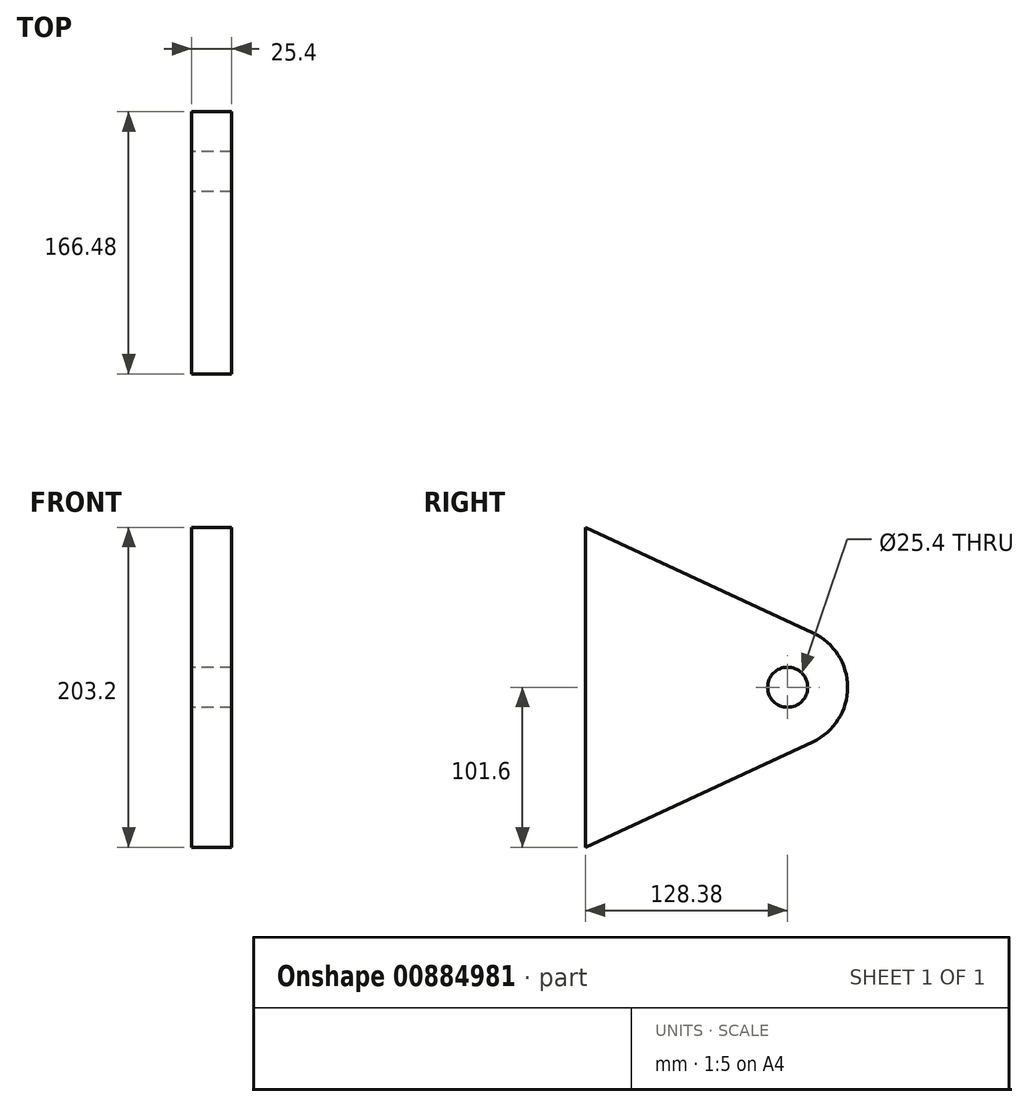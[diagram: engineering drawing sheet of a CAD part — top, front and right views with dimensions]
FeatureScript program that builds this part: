
annotation { "Feature Type Name" : "Feature", "Feature Type Description" : "" }
export const myFeature = defineFeature(function(context is Context, id is Id, definition is map)
    precondition{}
    {
        {
            var Q0;
            Q0=qCreatedBy(makeId("Right.planeOp"),FACE);
            var sketch = newSketch(context, id + "F0", { "sketchPlane" : qUnion([Q0])});
            skLineSegment(sketch, "E0", {"start": v(0, 101.6) * mm, "end": v(0, -101.6) * mm});
            skLineSegment(sketch, "E1", {"start": v(0, -101.6) * mm, "end": v(144.42, -34.56) * mm});
            skLineSegment(sketch, "E2", {"start": v(144.42, 34.56) * mm, "end": v(0, 101.6) * mm});
            skPoint(sketch, "E3.visualSharp", {"position": v(218.87, 0) * mm});
            skArc(sketch, "E3.filletArc", {"start": v(144.42, -34.56) * mm, "mid": v(166.48, 0) * mm, "end": v(144.42, 34.56) * mm});
            skCircle(sketch, "E4", {"center": v(128.38, 0) * mm, "radius": 12.7 * mm});
            skSolve(sketch);
        }
        {
            var Q0;
            Q0 = qSketchRegion(id + "F0", true);
            extrude(context, id + "F1", {"entities" : qUnion([Q0]), "depth" : 25.4 * mm, "offsetDistance" : 25.4 * mm});
        }
    });
